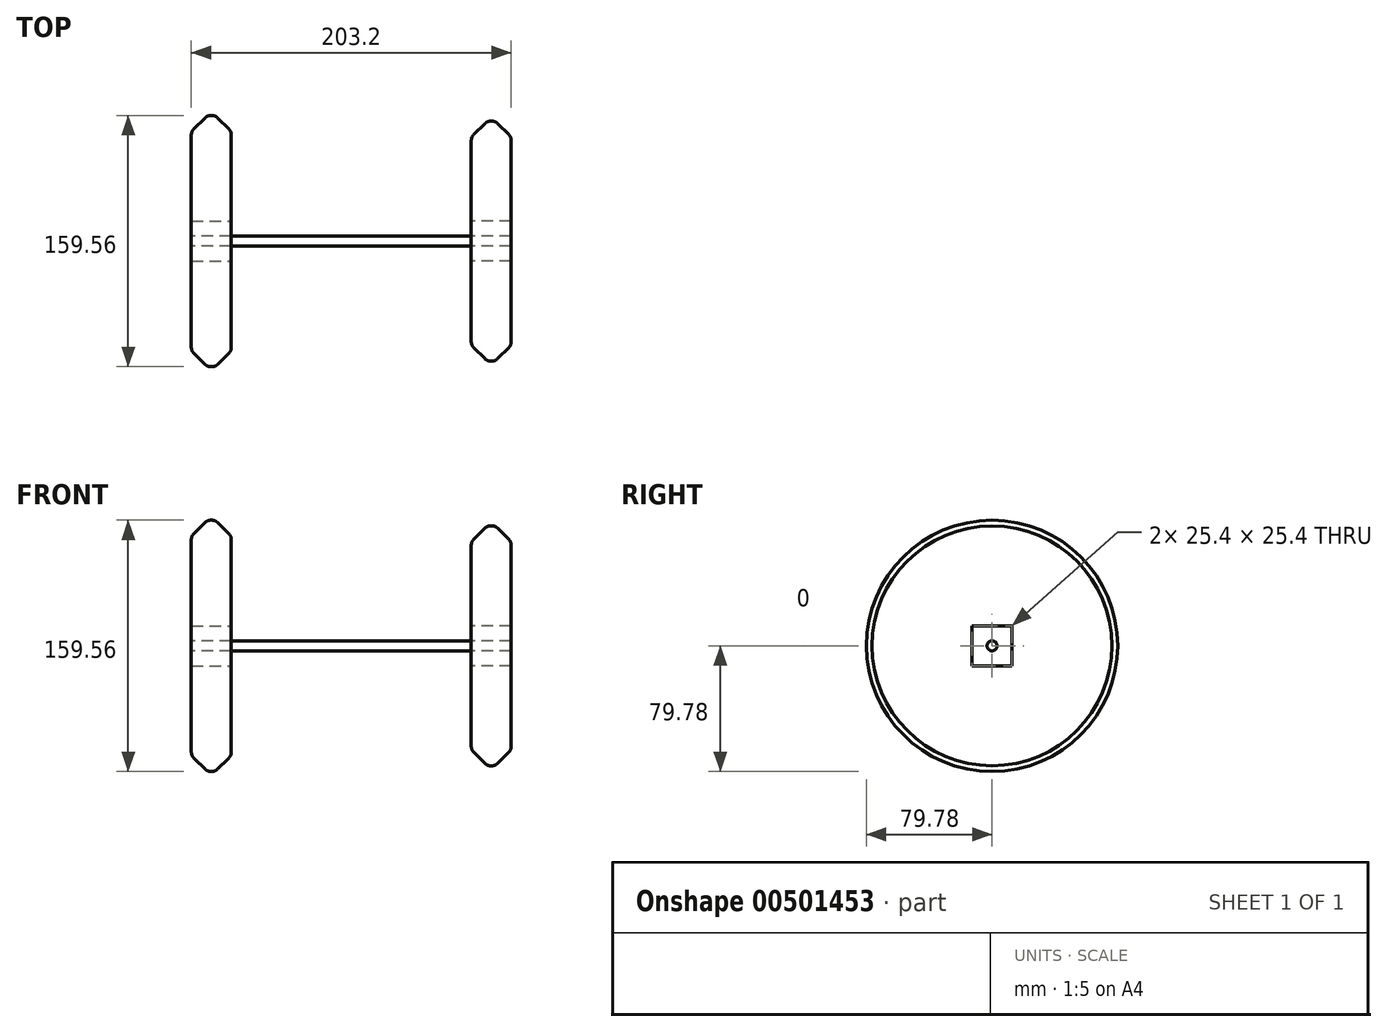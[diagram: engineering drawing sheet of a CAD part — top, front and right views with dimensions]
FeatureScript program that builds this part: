
annotation { "Feature Type Name" : "Feature", "Feature Type Description" : "" }
export const myFeature = defineFeature(function(context is Context, id is Id, definition is map)
    precondition{}
    {
        {
            var Q0;
            Q0=qCreatedBy(makeId("Right.planeOp"),FACE);
            cPlane(context, id + "F0", {"entities" : qUnion([Q0]), "cplaneType" : CPlaneType.OFFSET, "offset" : 76.2 * mm, "width" : 152.4 * mm, "height" : 152.4 * mm});
        }
        {
            var Q0;
            Q0=qCreatedBy(makeId("Right.planeOp"),FACE);
            cPlane(context, id + "F1", {"entities" : qUnion([Q0]), "cplaneType" : CPlaneType.OFFSET, "offset" : 76.2 * mm, "oppositeDirection" : true, "width" : 152.4 * mm, "height" : 152.4 * mm});
        }
        {
            var Q0;
            Q0=qCreatedBy(makeId("Right.planeOp"),FACE);
            var sketch = newSketch(context, id + "F2", { "sketchPlane" : qUnion([Q0])});
            skCircle(sketch, "E0", {"center": v(0, 0) * mm, "radius": 3.18 * mm});
            skSolve(sketch);
        }
        {
            var Q0;
            Q0=makeQuery(id+"F2.imprint","IMPRINT",FACE,{"disambiguationData":[TD([[makeQuery(id+"F2.imprint","IMPRINT",EDGE,{"derivedFrom":sQuery(id+"F2.wireOp",EDGE,"E0")}),1.0]])]});
            extrude(context, id + "F3", {"entities" : qUnion([Q0]), "endBound" : BoundingType.SYMMETRIC, "depth" : 203.2 * mm});
        }
        {
            var Q0;
            Q0=qCreatedBy(id+"F1.planeOp",FACE);
            var sketch = newSketch(context, id + "F4", { "sketchPlane" : qUnion([Q0])});
            skCircle(sketch, "E1", {"center": v(0, 0) * mm, "radius": 79.78 * mm});
            skLineSegment(sketch, "E2.bottom", {"start": v(12.7, 12.7) * mm, "end": v(-12.7, 12.7) * mm});
            skLineSegment(sketch, "E2.top", {"start": v(12.7, -12.7) * mm, "end": v(-12.7, -12.7) * mm});
            skLineSegment(sketch, "E2.left", {"start": v(12.7, 12.7) * mm, "end": v(12.7, -12.7) * mm});
            skLineSegment(sketch, "E2.right", {"start": v(-12.7, 12.7) * mm, "end": v(-12.7, -12.7) * mm});
            skSolve(sketch);
        }
        {
            var Q0;
            Q0=qCreatedBy(id+"F0.planeOp",FACE);
            var sketch = newSketch(context, id + "F5", { "sketchPlane" : qUnion([Q0])});
            skCircle(sketch, "E3", {"center": v(0, 0) * mm, "radius": 76.2 * mm});
            skLineSegment(sketch, "E4.bottom", {"start": v(-12.7, 12.7) * mm, "end": v(12.7, 12.7) * mm});
            skLineSegment(sketch, "E4.top", {"start": v(-12.7, -12.7) * mm, "end": v(12.7, -12.7) * mm});
            skLineSegment(sketch, "E4.left", {"start": v(-12.7, 12.7) * mm, "end": v(-12.7, -12.7) * mm});
            skLineSegment(sketch, "E4.right", {"start": v(12.7, 12.7) * mm, "end": v(12.7, -12.7) * mm});
            skSolve(sketch);
        }
        {
            var Q0;
            Q0=makeQuery(id+"F5.imprint","IMPRINT",FACE,{"disambiguationData":[TD([[makeQuery(id+"F5.imprint","IMPRINT",EDGE,{"derivedFrom":sQuery(id+"F5.wireOp",EDGE,"E3")}),1.0]])]});
            extrude(context, id + "F6", {"entities" : qUnion([Q0]), "depth" : 25.4 * mm});
        }
        {
            var Q0;
            Q0=makeQuery(id+"F4.imprint","IMPRINT",FACE,{"disambiguationData":[TD([[makeQuery(id+"F4.imprint","IMPRINT",EDGE,{"derivedFrom":sQuery(id+"F4.wireOp",EDGE,"E1")}),1.0]])]});
            extrude(context, id + "F7", {"entities" : qUnion([Q0]), "oppositeDirection" : true, "depth" : 25.4 * mm});
        }
        {
            var Q0;
            Q0=makeQuery(id+"F7.opExtrude","SWEPT_FACE",FACE,{"disambiguationData":[OSD([sQuery(id+"F4.wireOp",EDGE,"E1")])]});
            var Q1;
            Q1=makeQuery(id+"F6.opExtrude","SWEPT_FACE",FACE,{"disambiguationData":[OSD([sQuery(id+"F5.wireOp",EDGE,"E3")])]});
            chamfer(context, id + "F8", {"entities" : qUnion([Q0, Q1]), "width" : 10.16 * mm, "tangentPropagation" : true});
        }
        {
            var Q0;
            Q0=makeQuery(id+"F7.opExtrude","SWEPT_FACE",FACE,{"disambiguationData":[OSD([sQuery(id+"F4.wireOp",EDGE,"E1")])]});
            var Q1;
            {var subQ0=sQuery(id+"F4.wireOp",EDGE,"E1");Q1=makeQuery(id+"F8.opChamfer","BLEND_EDGE",EDGE,{"blendedFrom":[makeQuery(id+"F7.opExtrude","CAP_EDGE",EDGE,{"disambiguationData":[OSD([subQ0])],"isStart":false}),makeQuery(id+"F7.opExtrude","CAP_FACE",FACE,{"disambiguationData":[OSD([subQ0,sQuery(id+"F4.wireOp",EDGE,"E2.bottom"),sQuery(id+"F4.wireOp",EDGE,"E2.top"),sQuery(id+"F4.wireOp",EDGE,"E2.left"),sQuery(id+"F4.wireOp",EDGE,"E2.right")])],"isStart":false})],"blendedInto":[makeQuery(id+"F7.opExtrude","CAP_FACE",FACE,{"disambiguationData":[OSD([subQ0,sQuery(id+"F4.wireOp",EDGE,"E2.bottom"),sQuery(id+"F4.wireOp",EDGE,"E2.top"),sQuery(id+"F4.wireOp",EDGE,"E2.left"),sQuery(id+"F4.wireOp",EDGE,"E2.right")])],"isStart":false})]});}
            var Q2;
            {var subQ0=sQuery(id+"F4.wireOp",EDGE,"E1");Q2=makeQuery(id+"F8.opChamfer","BLEND_EDGE",EDGE,{"blendedFrom":[makeQuery(id+"F7.opExtrude","CAP_EDGE",EDGE,{"disambiguationData":[OSD([subQ0])],"isStart":true}),makeQuery(id+"F7.opExtrude","CAP_FACE",FACE,{"disambiguationData":[OSD([subQ0,sQuery(id+"F4.wireOp",EDGE,"E2.bottom"),sQuery(id+"F4.wireOp",EDGE,"E2.top"),sQuery(id+"F4.wireOp",EDGE,"E2.left"),sQuery(id+"F4.wireOp",EDGE,"E2.right")])],"isStart":true})],"blendedInto":[makeQuery(id+"F7.opExtrude","CAP_FACE",FACE,{"disambiguationData":[OSD([subQ0,sQuery(id+"F4.wireOp",EDGE,"E2.bottom"),sQuery(id+"F4.wireOp",EDGE,"E2.top"),sQuery(id+"F4.wireOp",EDGE,"E2.left"),sQuery(id+"F4.wireOp",EDGE,"E2.right")])],"isStart":true})]});}
            var Q3;
            {var subQ0=sQuery(id+"F5.wireOp",EDGE,"E3");Q3=makeQuery(id+"F8.opChamfer","BLEND_EDGE",EDGE,{"blendedFrom":[makeQuery(id+"F6.opExtrude","CAP_EDGE",EDGE,{"disambiguationData":[OSD([subQ0])],"isStart":true}),makeQuery(id+"F6.opExtrude","SWEPT_FACE",FACE,{"disambiguationData":[OSD([subQ0])]})],"blendedInto":[makeQuery(id+"F6.opExtrude","SWEPT_FACE",FACE,{"disambiguationData":[OSD([subQ0])]})]});}
            var Q4;
            {var subQ0=sQuery(id+"F5.wireOp",EDGE,"E3");Q4=makeQuery(id+"F8.opChamfer","BLEND_EDGE",EDGE,{"blendedFrom":[makeQuery(id+"F6.opExtrude","CAP_EDGE",EDGE,{"disambiguationData":[OSD([subQ0])],"isStart":false}),makeQuery(id+"F6.opExtrude","SWEPT_FACE",FACE,{"disambiguationData":[OSD([subQ0])]})],"blendedInto":[makeQuery(id+"F6.opExtrude","SWEPT_FACE",FACE,{"disambiguationData":[OSD([subQ0])]})]});}
            var Q5;
            {var subQ0=sQuery(id+"F5.wireOp",EDGE,"E3");Q5=makeQuery(id+"F8.opChamfer","BLEND_EDGE",EDGE,{"blendedFrom":[makeQuery(id+"F6.opExtrude","CAP_EDGE",EDGE,{"disambiguationData":[OSD([subQ0])],"isStart":false}),makeQuery(id+"F6.opExtrude","CAP_FACE",FACE,{"disambiguationData":[OSD([subQ0,sQuery(id+"F5.wireOp",EDGE,"E4.bottom"),sQuery(id+"F5.wireOp",EDGE,"E4.top"),sQuery(id+"F5.wireOp",EDGE,"E4.left"),sQuery(id+"F5.wireOp",EDGE,"E4.right")])],"isStart":false})],"blendedInto":[makeQuery(id+"F6.opExtrude","CAP_FACE",FACE,{"disambiguationData":[OSD([subQ0,sQuery(id+"F5.wireOp",EDGE,"E4.bottom"),sQuery(id+"F5.wireOp",EDGE,"E4.top"),sQuery(id+"F5.wireOp",EDGE,"E4.left"),sQuery(id+"F5.wireOp",EDGE,"E4.right")])],"isStart":false})]});}
            var Q6;
            {var subQ0=sQuery(id+"F5.wireOp",EDGE,"E3");Q6=makeQuery(id+"F8.opChamfer","BLEND_FACE",FACE,{"disambiguationData":[OSD([subQ0]),TDD([makeQuery(id+"F6.opExtrude","CAP_EDGE",EDGE,{"disambiguationData":[OSD([subQ0])],"isStart":true})])]});}
            fillet(context, id + "F9", {"entities" : qUnion([Q0, Q1, Q2, Q3, Q4, Q5, Q6]), "radius" : 5.08 * mm, "tangentPropagation" : true, "allowEdgeOverflow" : false});
        }
    });
